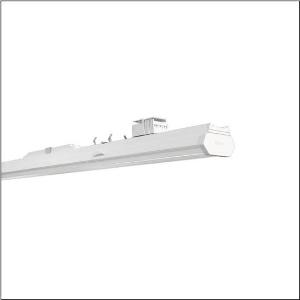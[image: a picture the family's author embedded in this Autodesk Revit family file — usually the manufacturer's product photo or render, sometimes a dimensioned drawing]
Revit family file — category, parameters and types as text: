
# Revit family: licross_r__11_protected_tw_51tp12tnt85x_7ce4
name_source: partatom
category: Lighting Fixtures
units: mm (PartAtom-declared; Revit-internal decimal feet)

## family parameters
Cut with Voids When Loaded = No
Host = Face
Light Source = No
Part Type = Normal
Room Calculation Point = No
Round Connector Dimension = Use Diameter
Shared = No

## types (1)
- --- (1 x LED 2700 K ... 6500 K, 8840 lm, 56 W, 2700K)
    Apparent Load = 56 VA
    CIE Flux Codes = 70 91 97 98 100
    Color Rendering = 80
    Color Temperature = 2700K
    Default Elevation = 1800 mm
    Description = Licross® 11 Protected TW, luminaire insert, of sheet steel, galvanised, coil coated, white, length: 1.500mm, width: 90mm, height: 101mm, LED rated luminous flux: 8.840lm, light colour: 8tw, control gear: DALI DT8, with plug, 5-pole, with phase selection, mains connection: 220..240V, AC, 50/60Hz, rated input power: 56W, halogen-free wiring, primary optical cover: cover, of PMMA, light emission: direct distribution, primary light characteristic: symmetric, protection rating (complete): IP64, insulation class (complete): insulation class I (protective earthing), certification: CE, ENEC, VDE, UKCA, protection symbol: D if used in an environment with conductive dust loads with corresponding accessories, impact resistance: IK06, permissible ambient temperature for indoor applications: -25..+35°C, corresponds to IFS (International Featured Standards) requirements for safety and quality in the food industry, reducing of maximum allowable ambient temperature of 5°C with ceiling mounting, LABS conformity tested according to VDMA 24364:2018-05, packaging unit: 1 piece
    Height = 92 mm
    Lamp = 1 x LED 2700 K ... 6500 K
    Lamp Light Flux = 8840 lm
    Lamp Power = 56 W
    Lamp count = 1
    Length = 1500 mm
    Luminous efficacy = 158 lm/W
    Manufacturer = Siteco
    ModVariant = No
    Model = 51TP12TNT85X
    Mounting Place = Ceiling
    Mounting Type = Pendant
    Number of Poles = 1
    OnlyDefault = Yes
    Power Factor = 1
    Product Name = Licross® 11 Protected TW
    Product group = luminaire insert
    ProductGroupID = 901
    Protection Class = Protection class I
    Protection Degree = IP 64
    RLX_Detail_Level = 1
    RLX_Emergency_Light_Flux = 0 lm
    RLX_Emergency_Type = 0
    RLX_Emergency_Type_DB = No
    RlxData = <blob elided: 20641 chars, md5=0a9b0147>
    Socket = socket
    Standby Power = 0 W
    System Light Flux = 8840 lm
    System Power = 56 W
    Type Comments = individual setting: CCT=2700K
    Type Image = l_1256148.jpg
    URL = http://relux.com
    VarID = @adj_006907
    Voltage = 0 V
    Weight = 0.00 kg
    Width = 88 mm

## geometry (parser evidence)
native form markers: Blend x4, Sweep x11
no freeform markers — native parametric forms only
